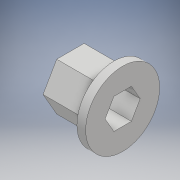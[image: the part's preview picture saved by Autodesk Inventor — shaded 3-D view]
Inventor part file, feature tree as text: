
AUTODESK INVENTOR PART (.ipt)
format: ipt  version: 2018 (Build 220112000, 112)  size: 172,032 bytes
history: native  units: mm
features: sketch x11, extrude x8
ambient origin geometry x8: Origin, YZ Plane, XZ Plane, XY Plane, X Axis, Y Axis, Z Axis, Center Point
bodies: Solid1 (feature_tree)
feature tree (19):
  extrude  "Extrusion1"  Depth=3.0mm
  sketch  "Sketch2"  dims[d2=3.0mm d3=0.0mm d4=2.0mm d5=0.0mm]
  extrude  "Extrusion2"  Depth=2.0mm TaperAngle=0.0deg
  sketch  "Sketch4"  dims[d11=17.0mm d12=2.0mm d13=0.0mm]
  extrude  "Extrusion3"  Depth=10.0mm TaperAngle=0.0deg
  sketch  "Sketch6"  dims[d18=12.6mm d19=10.0mm d20=0.0mm]
  extrude  "Extrusion4"  Depth=2.0mm TaperAngle=0.0deg
  extrude  "Extrusion5"  Depth=5.0mm TaperAngle=0.0deg
  extrude  "Extrusion6"  Depth=10.0mm TaperAngle=0.0deg
  extrude  "Extrusion7"  [1 undecoded]
  extrude  "Extrusion8"  [1 undecoded]
  sketch  "Sketch1"  dims[d0=3.0mm d1=3.0mm]
  sketch  "Sketch3"  dims[d6=10.0mm d7=0.0mm d9=10.0mm d10=0.0mm]
  sketch  "Sketch5"  dims[d14=17.25mm d15=0.0mm d16=5.0mm d17=0.0mm]
  sketch  "Sketch7"
  sketch  "Sketch8"
  sketch  "Sketch9"
  sketch  "Sketch10"
  sketch  "Sketch11"
note: 2 required parameter values undecoded (feature->parameter linkage not recoverable at this tier; creation-order binding heuristic only, values carry confidence <= 0.55)
